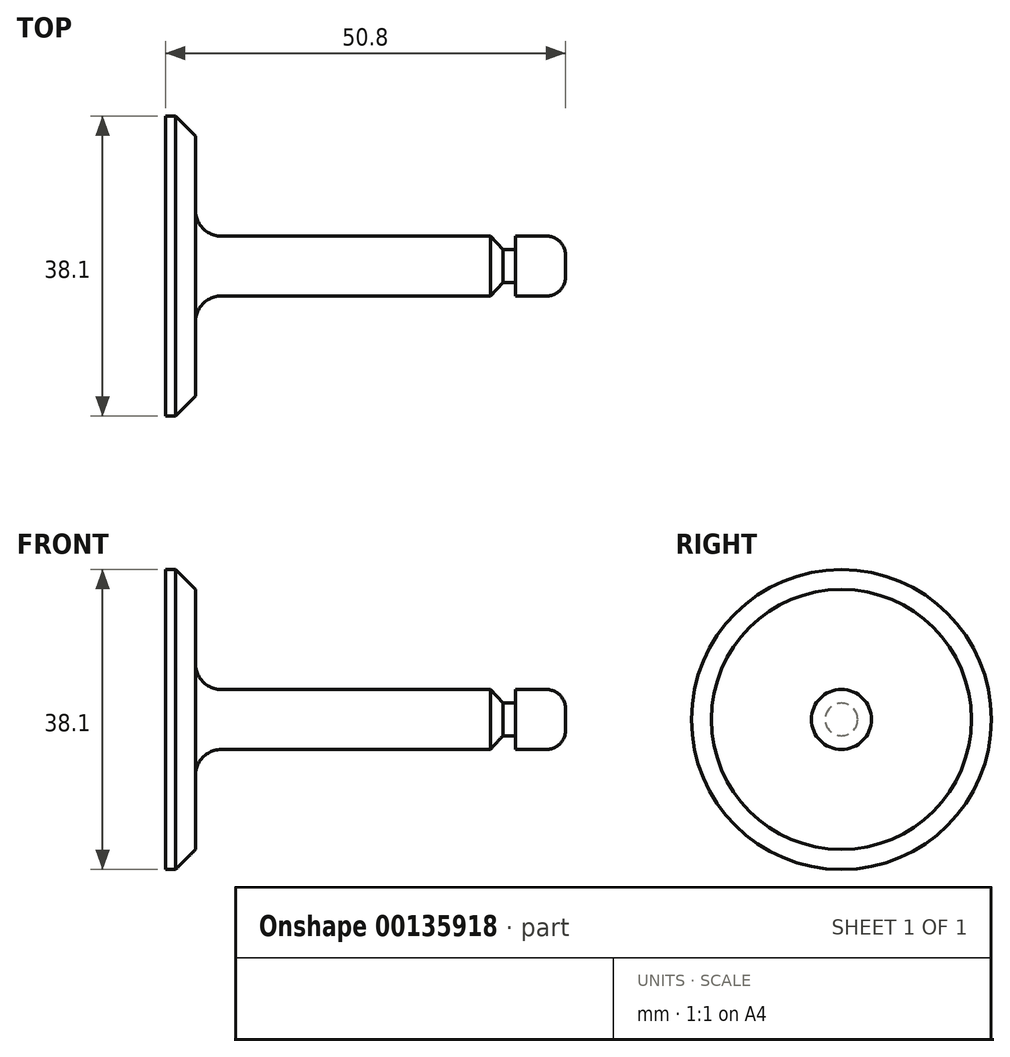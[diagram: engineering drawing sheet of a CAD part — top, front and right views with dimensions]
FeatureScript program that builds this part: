
annotation { "Feature Type Name" : "Feature", "Feature Type Description" : "" }
export const myFeature = defineFeature(function(context is Context, id is Id, definition is map)
    precondition{}
    {
        {
            var Q0;
            Q0=qCreatedBy(makeId("Front.planeOp"),FACE);
            var sketch = newSketch(context, id + "F0", { "sketchPlane" : qUnion([Q0])});
            skLineSegment(sketch, "E0", {"start": v(0, 0) * mm, "end": v(-50.8, 0) * mm});
            skLineSegment(sketch, "E1", {"start": v(-50.8, 0) * mm, "end": v(-50.8, 19.05) * mm});
            skLineSegment(sketch, "E2", {"start": v(0, 0) * mm, "end": v(0, 3.81) * mm});
            skLineSegment(sketch, "E3", {"start": v(-50.8, 19.05) * mm, "end": v(-47, 19.05) * mm});
            skLineSegment(sketch, "E4", {"start": v(-47, 7.06) * mm, "end": v(-47, 19.05) * mm});
            skLineSegment(sketch, "E5", {"start": v(0, 3.81) * mm, "end": v(-6.35, 3.81) * mm});
            skPoint(sketch, "E6.visualSharp", {"position": v(-47, 3.81) * mm});
            skArc(sketch, "E6.filletArc", {"start": v(-47, 7.06) * mm, "mid": v(-46.04, 4.76) * mm, "end": v(-43.74, 3.81) * mm});
            skLineSegment(sketch, "E7", {"start": v(-6.35, 3.8) * mm, "end": v(-6.35, 2.07) * mm});
            skLineSegment(sketch, "E8", {"start": v(-6.35, 2.07) * mm, "end": v(-7.95, 2.07) * mm});
            skLineSegment(sketch, "E9", {"start": v(-7.95, 2.07) * mm, "end": v(-9.55, 3.8) * mm});
            skLineSegment(sketch, "E10", {"start": v(-43.74, 3.81) * mm, "end": v(-9.55, 3.8) * mm});
            skSolve(sketch);
        }
        {
            var Q0;
            Q0=makeQuery(id+"F0.imprint","IMPRINT",FACE,{"disambiguationData":[TD([[makeQuery(id+"F0.imprint","IMPRINT",EDGE,{"derivedFrom":sQuery(id+"F0.wireOp",EDGE,"E0")}),-1.0]])]});
            var Q1;
            Q1=sQuery(id+"F0.wireOp",EDGE,"E0");
            revolve(context, id + "F1", {"entities" : qUnion([Q0]), "axis" : qUnion([Q1]), "revolveType" : RevolveType.FULL});
        }
        {
            var Q0;
            Q0=makeQuery(id+"F1.opRevolve","SWEPT_EDGE",EDGE,{"disambiguationData":[OSD([sQuery(id+"F0.wireOp",EDGE,"E3"),sQuery(id+"F0.wireOp",EDGE,"E4")])]});
            chamfer(context, id + "F2", {"entities" : qUnion([Q0]), "chamferType" : ChamferType.OFFSET_ANGLE, "width" : 2.54 * mm, "oppositeDirection" : true, "angle" : 45 * degree, "tangentPropagation" : true});
        }
        {
            var Q0;
            Q0=makeQuery(id+"F1.opRevolve","SWEPT_FACE",FACE,{"disambiguationData":[OSD([sQuery(id+"F0.wireOp",EDGE,"E2")])]});
            fillet(context, id + "F3", {"entities" : qUnion([Q0]), "radius" : 2.44 * mm, "tangentPropagation" : true, "allowEdgeOverflow" : false});
        }
    });
